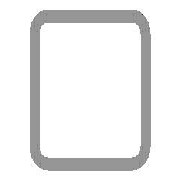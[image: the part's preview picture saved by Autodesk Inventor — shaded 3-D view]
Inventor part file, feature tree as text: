
AUTODESK INVENTOR PART (.ipt)
format: ipt  version: 2025.3 (Build 293356000, 356)  size: 133,632 bytes
history: native  units: mm (DEFAULTED — no unit token found)
features: other x4, sketch x1, plane x1
ambient origin geometry x8: Origin, YZ Plane, XZ Plane, XY Plane, X Axis, Y Axis, Z Axis, Center Point
bodies: Solid1 (feature_tree), Body (feature_tree)
feature tree (6):
  parser-record x1  (decoder bookkeeping rows leaked as tree rows — omitted from the tree; the rows remain in map.json)
  other  "Driven Length"
  other  "Start Plane"
  other  "End Plane"
  sketch  "Sketch3"  dims[d3=5400.0mm d4=0.0mm d7=6.0mm d9=80.0mm d11=80.0mm d12=3.0mm d13=-0.0mm d14=5400.0mm d15=40.0mm d16=40.0mm d17=90.0deg d18=5400.0mm]
  plane  "Work Plane3"
